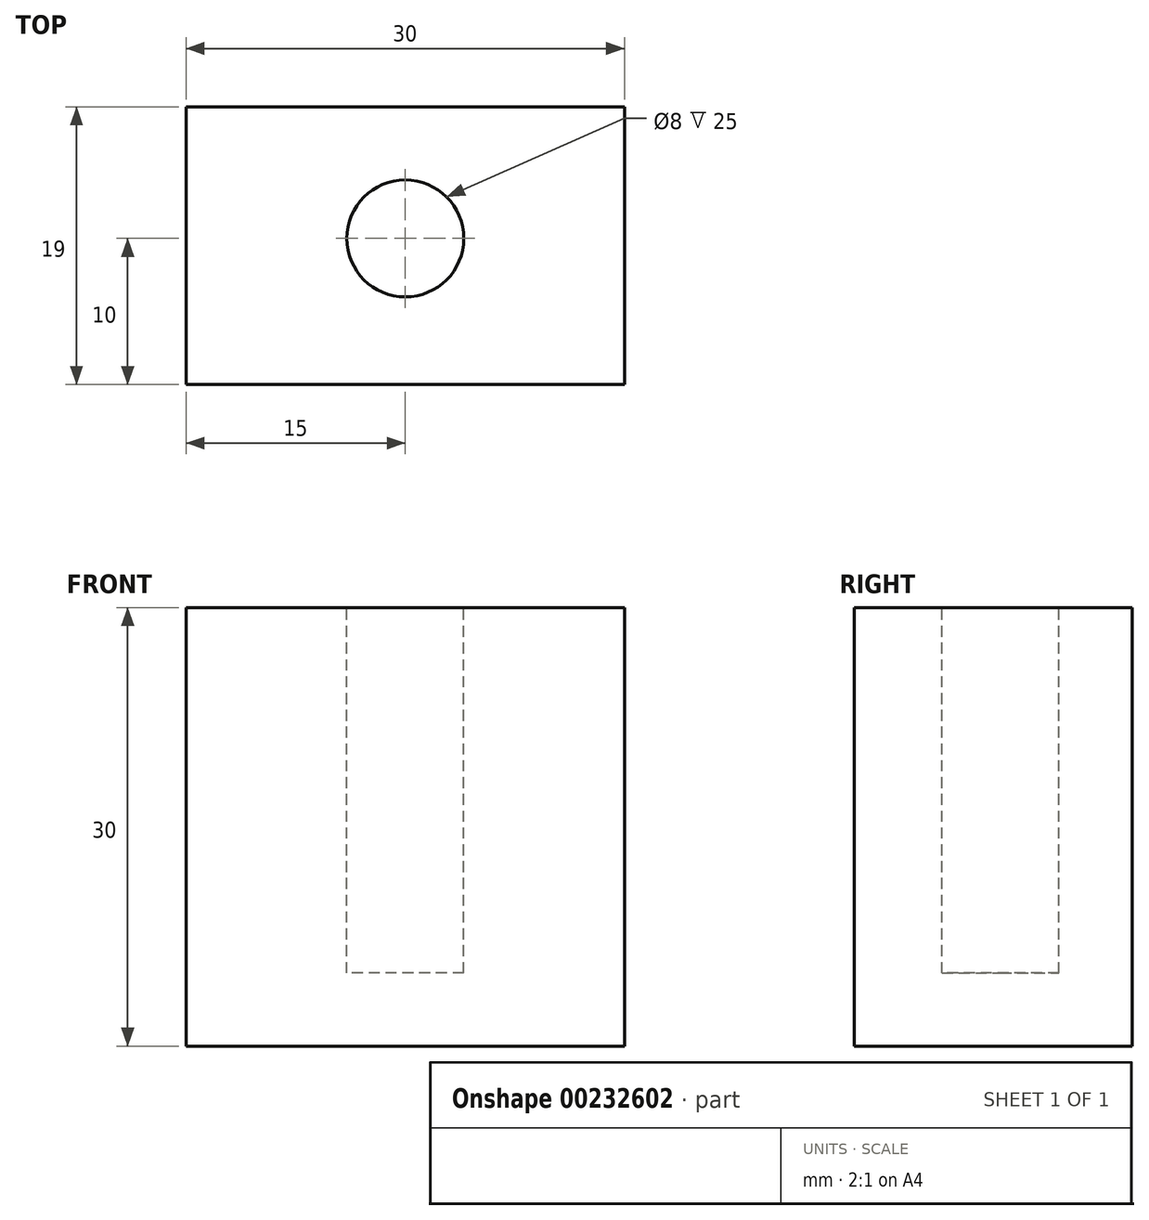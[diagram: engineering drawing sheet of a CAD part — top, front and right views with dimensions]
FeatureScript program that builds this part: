
annotation { "Feature Type Name" : "Feature", "Feature Type Description" : "" }
export const myFeature = defineFeature(function(context is Context, id is Id, definition is map)
    precondition{}
    {
        {
            var Q0;
            Q0=qCreatedBy(makeId("Right.planeOp"),FACE);
            var sketch = newSketch(context, id + "F0", { "sketchPlane" : qUnion([Q0])});
            skLineSegment(sketch, "E0.bottom", {"start": v(0, 0) * mm, "end": v(19, 0) * mm});
            skLineSegment(sketch, "E0.top", {"start": v(0, 30) * mm, "end": v(19, 30) * mm});
            skLineSegment(sketch, "E0.left", {"start": v(0, 0) * mm, "end": v(0, 30) * mm});
            skLineSegment(sketch, "E0.right", {"start": v(19, 0) * mm, "end": v(19, 30) * mm});
            skSolve(sketch);
        }
        {
            var Q0;
            Q0 = qSketchRegion(id + "F0", true);
            extrude(context, id + "F1", {"entities" : qUnion([Q0]), "depth" : 30 * mm});
        }
        {
            var Q0;
            Q0=makeQuery(id+"F1.opExtrude","SWEPT_FACE",FACE,{"disambiguationData":[OSD([sQuery(id+"F0.wireOp",EDGE,"E0.top")])]});
            var sketch = newSketch(context, id + "F2", { "sketchPlane" : qUnion([Q0])});
            skCircle(sketch, "E1", {"center": v(15, 10) * mm, "radius": 4 * mm});
            skSolve(sketch);
        }
        {
            var Q0;
            Q0 = qSketchRegion(id + "F2", true);
            extrude(context, id + "F3", {"entities" : qUnion([Q0]), "operationType" : NewBodyOperationType.REMOVE, "oppositeDirection" : true, "depth" : 25 * mm});
        }
    });
